# Revit family: Furniture-Lighted_Mirror-KOHLER-FOREFRONT-K-29155IN_1
name_source: partatom
category: Lighting Fixtures
revit_build: Autodesk Revit 2017 (Build: 20160225_1515(x64)
units: mm (PartAtom-declared; Revit-internal decimal feet)

## family parameters
Cut with Voids When Loaded = No
Host = Face
Light Source = Yes
OmniClass Number = 23.21.37.13.15
OmniClass Title = Mirrors
Part Type = Normal
Room Calculation Point = No
Round Connector Dimension = Use Diameter
Shared = No

## types (1)
- NA-Anodized Aluminum
    ADA Compliant = No
    Apparent Load = 250 VA
    Assembly Code = D5020200
    Color Filter = 16777215
    Date Modified = 06/07/2021
    Default Elevation = 60"
    Description = Lite Mirror 720mm
    Dimming Lamp Color Temperature Shift = Incandescent Lamp Curve
    Electrical Connector = Yes
    Electrical Note = One Circuit Required
    Emit from Line Length = 23 5/8"
    Finish = Kohler-Metal-NA-Anodized_Aluminum
    Height = 25 9/16"
    Lamp = LED
    Length = 1 1/8"
    Light Source Symbol Size = 16"
    Manufacturer = KOHLER Co.
    Master Format 2014 = 10 28 16
    Master Format 2014 Name = Bath Accessories
    Material = Anodized Aluminum Construction
    Model = K-29155IN-NA
    Product Name = FOREFRONT
    Type = 1
    URL = https://www.kohler.co.in
    Voltage = 12 V
    WaterSense Certified = No
    Wattage Comments = 170-250 VAC
    Width = 28 3/8"

## geometry (parser evidence)
native form markers: Sweep x3
no freeform markers — native parametric forms only
